# Revit family: Brighton
name_source: partatom
category: Lighting Fixtures
revit_build: Autodesk Revit 2014 (Build: 20130308_1515(x64)
units: mm (PartAtom-declared; Revit-internal decimal feet)

## types (1)
- T5
    Apparent Load = 55 VA
    Assembly Code = D5020280
    CRI = 70
    Certification = Listed to UL8750 , UL1598 and CSA22.2#250.13-14 for wet locations
    Color Filter = 16777215
    Controls = On/Off,Scheduled Dimming,Luminaire Grouping,Occupancy Detection,Dusk to Dawn Operation
    Default Elevation = 48 "
    Description = The crowned top of the Brighton T5 lends a transitional feel to the modular Village Collection Series of decorative post tops. The Village Collection Series has over 80 different configurable combinations available for lighting designers and architects to create the perfect post top for their environment.
    Dimming Lamp Color Temperature Shift = <None>
    Emit Shape Visible in Rendering = No
    Emit from Circle Diameter = 10 "
    Finish = Metal-Hubbell-Galvanized_Steel
    Glass = Hubbell-Glass
    IP Rating = IP55
    Lamp = LED
    Light Distribution = IES Type II,III,IV
    Lighting Connector Description = Lighting Connector
    Load Classification = Lighting
    Manufacturer = Beacon
    Model = T5 Brighton
    Photometric Web File = generic
    Power Factor = 1
    Product Documentation Link = https://hubbellcdn.com
    Product Page URL = https://www.hubbell.com
    Sensor Type = Passive infrared with Photoresistor
    Tilt Angle = 60.00°
    Type Comments = Light Fixture
    URL = https://www.hubbell.com
    Voltage = 120 V
    Warranty = 5 Year Limited Warranty
    Wattage Comments = 55W
    Watts = 55 W

## geometry (parser evidence)
native form markers: Blend x29, Sweep x5
no freeform markers — native parametric forms only
